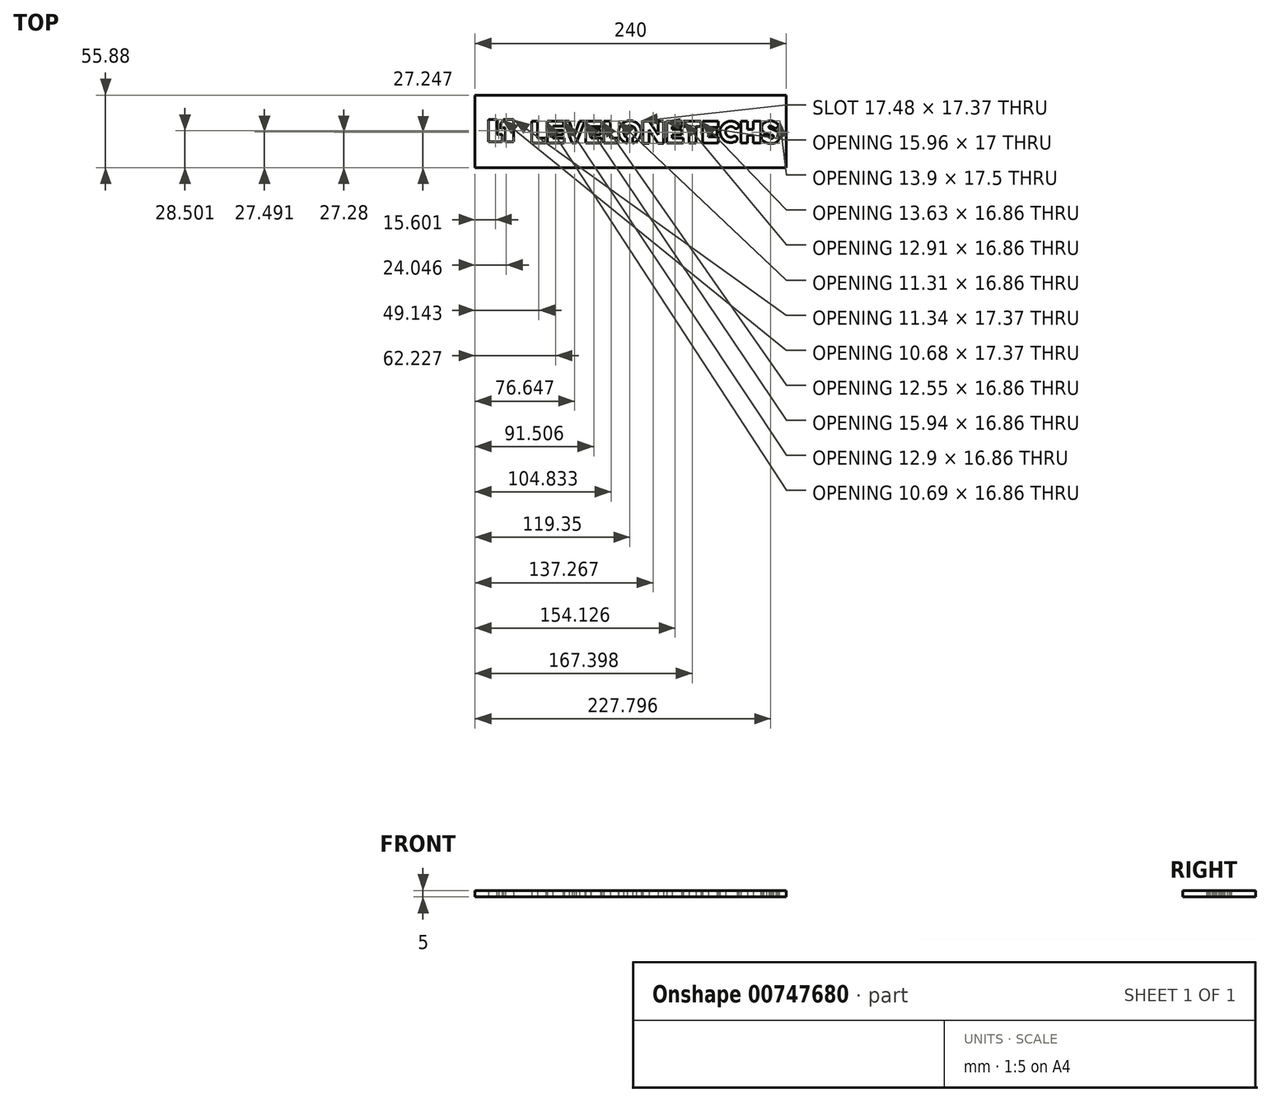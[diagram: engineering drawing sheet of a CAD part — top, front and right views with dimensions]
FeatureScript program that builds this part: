
annotation { "Feature Type Name" : "Feature", "Feature Type Description" : "" }
export const myFeature = defineFeature(function(context is Context, id is Id, definition is map)
    precondition{}
    {
        {
            var Q0;
            Q0=qCreatedBy(makeId("Top.planeOp"),FACE);
            var sketch = newSketch(context, id + "F0", { "sketchPlane" : qUnion([Q0])});
            skLineSegment(sketch, "E0.bottom", {"start": v(-121.3, 38.56) * mm, "end": v(118.7, 38.56) * mm});
            skLineSegment(sketch, "E0.top", {"start": v(-121.3, -17.32) * mm, "end": v(118.7, -17.32) * mm});
            skLineSegment(sketch, "E0.left", {"start": v(-121.3, 38.56) * mm, "end": v(-121.3, -17.32) * mm});
            skLineSegment(sketch, "E0.right", {"start": v(118.7, 38.56) * mm, "end": v(118.7, -17.32) * mm});
            skLineSegment(sketch, "E1", {"start": v(-77.5, 18.43) * mm, "end": v(-77.5, 1.57) * mm});
            skLineSegment(sketch, "E2", {"start": v(-77.5, 1.57) * mm, "end": v(-66.81, 1.57) * mm});
            skLineSegment(sketch, "E3", {"start": v(-66.81, 1.57) * mm, "end": v(-66.81, 5.44) * mm});
            skLineSegment(sketch, "E4", {"start": v(-66.81, 5.44) * mm, "end": v(-73.26, 5.44) * mm});
            skLineSegment(sketch, "E5", {"start": v(-73.26, 5.44) * mm, "end": v(-73.26, 18.43) * mm});
            skLineSegment(sketch, "E6", {"start": v(-73.26, 18.43) * mm, "end": v(-77.5, 18.43) * mm});
            skLineSegment(sketch, "E7", {"start": v(-65.52, 18.43) * mm, "end": v(-65.52, 1.57) * mm});
            skLineSegment(sketch, "E8", {"start": v(-65.52, 1.57) * mm, "end": v(-52.62, 1.57) * mm});
            skLineSegment(sketch, "E9", {"start": v(-52.62, 1.57) * mm, "end": v(-52.62, 5.44) * mm});
            skLineSegment(sketch, "E10", {"start": v(-52.62, 5.44) * mm, "end": v(-61.28, 5.44) * mm});
            skLineSegment(sketch, "E11", {"start": v(-61.28, 5.44) * mm, "end": v(-61.28, 8.02) * mm});
            skLineSegment(sketch, "E12", {"start": v(-61.28, 8.02) * mm, "end": v(-53.64, 8.02) * mm});
            skLineSegment(sketch, "E13", {"start": v(-53.64, 8.02) * mm, "end": v(-53.64, 11.61) * mm});
            skLineSegment(sketch, "E14", {"start": v(-53.64, 11.61) * mm, "end": v(-61.38, 11.61) * mm});
            skLineSegment(sketch, "E15", {"start": v(-61.38, 11.61) * mm, "end": v(-61.38, 14.56) * mm});
            skLineSegment(sketch, "E16", {"start": v(-61.38, 14.56) * mm, "end": v(-53.17, 14.56) * mm});
            skLineSegment(sketch, "E17", {"start": v(-53.17, 14.56) * mm, "end": v(-53.17, 18.43) * mm});
            skLineSegment(sketch, "E18", {"start": v(-53.17, 18.43) * mm, "end": v(-65.52, 18.43) * mm});
            skLineSegment(sketch, "E19", {"start": v(-52.62, 18.43) * mm, "end": v(-46.63, 1.57) * mm});
            skLineSegment(sketch, "E20", {"start": v(-46.63, 1.57) * mm, "end": v(-43.4, 1.57) * mm});
            skLineSegment(sketch, "E21", {"start": v(-43.4, 1.57) * mm, "end": v(-36.68, 18.43) * mm});
            skLineSegment(sketch, "E22", {"start": v(-36.68, 18.43) * mm, "end": v(-40.74, 18.43) * mm});
            skLineSegment(sketch, "E23", {"start": v(-40.74, 18.43) * mm, "end": v(-44.98, 7.19) * mm});
            skLineSegment(sketch, "E24", {"start": v(-44.98, 7.19) * mm, "end": v(-48.75, 18.43) * mm});
            skLineSegment(sketch, "E25", {"start": v(-48.75, 18.43) * mm, "end": v(-52.62, 18.43) * mm});
            skLineSegment(sketch, "E26", {"start": v(-36.07, 18.43) * mm, "end": v(-36.07, 1.57) * mm});
            skLineSegment(sketch, "E27", {"start": v(-36.07, 1.57) * mm, "end": v(-23.52, 1.57) * mm});
            skLineSegment(sketch, "E28", {"start": v(-23.52, 1.57) * mm, "end": v(-23.52, 5.44) * mm});
            skLineSegment(sketch, "E29", {"start": v(-23.52, 5.44) * mm, "end": v(-31.89, 5.44) * mm});
            skLineSegment(sketch, "E30", {"start": v(-31.89, 5.44) * mm, "end": v(-31.89, 7.83) * mm});
            skLineSegment(sketch, "E31", {"start": v(-31.89, 7.83) * mm, "end": v(-24.56, 7.83) * mm});
            skLineSegment(sketch, "E32", {"start": v(-24.56, 7.83) * mm, "end": v(-24.56, 11.98) * mm});
            skLineSegment(sketch, "E33", {"start": v(-24.56, 11.98) * mm, "end": v(-32.27, 11.98) * mm});
            skLineSegment(sketch, "E34", {"start": v(-32.27, 11.98) * mm, "end": v(-32.27, 14.34) * mm});
            skLineSegment(sketch, "E35", {"start": v(-32.27, 14.34) * mm, "end": v(-23.6, 14.34) * mm});
            skLineSegment(sketch, "E36", {"start": v(-23.6, 14.34) * mm, "end": v(-23.6, 18.43) * mm});
            skLineSegment(sketch, "E37", {"start": v(-23.6, 18.43) * mm, "end": v(-36.07, 18.43) * mm});
            skLineSegment(sketch, "E38", {"start": v(-111.04, 19.86) * mm, "end": v(-111.04, 2.5) * mm});
            skLineSegment(sketch, "E39", {"start": v(-111.04, 2.5) * mm, "end": v(-100.36, 2.5) * mm});
            skLineSegment(sketch, "E40", {"start": v(-100.36, 2.5) * mm, "end": v(-100.36, 8.47) * mm});
            skLineSegment(sketch, "E41", {"start": v(-100.36, 8.47) * mm, "end": v(-104.65, 8.47) * mm});
            skLineSegment(sketch, "E42", {"start": v(-104.65, 8.47) * mm, "end": v(-104.65, 19.86) * mm});
            skLineSegment(sketch, "E43", {"start": v(-104.65, 19.86) * mm, "end": v(-111.04, 19.86) * mm});
            skLineSegment(sketch, "E44", {"start": v(-91.58, 2.5) * mm, "end": v(-91.58, 19.86) * mm});
            skLineSegment(sketch, "E45", {"start": v(-91.58, 19.86) * mm, "end": v(-99.58, 19.86) * mm});
            skLineSegment(sketch, "E46", {"start": v(-99.58, 19.86) * mm, "end": v(-102.92, 13.24) * mm});
            skLineSegment(sketch, "E47", {"start": v(-102.92, 13.24) * mm, "end": v(-98.09, 13.24) * mm});
            skLineSegment(sketch, "E48", {"start": v(-98.09, 13.24) * mm, "end": v(-98.09, 2.5) * mm});
            skLineSegment(sketch, "E49", {"start": v(-98.09, 2.5) * mm, "end": v(-91.58, 2.5) * mm});
            skLineSegment(sketch, "E50", {"start": v(-22.12, 18.43) * mm, "end": v(-22.12, 1.57) * mm});
            skLineSegment(sketch, "E51", {"start": v(-22.12, 1.57) * mm, "end": v(-10.81, 1.57) * mm});
            skLineSegment(sketch, "E52", {"start": v(-10.81, 1.57) * mm, "end": v(-10.81, 5.46) * mm});
            skLineSegment(sketch, "E53", {"start": v(-10.81, 5.46) * mm, "end": v(-16.93, 5.46) * mm});
            skLineSegment(sketch, "E54", {"start": v(-16.93, 5.46) * mm, "end": v(-16.93, 18.43) * mm});
            skLineSegment(sketch, "E55", {"start": v(-16.93, 18.43) * mm, "end": v(-22.12, 18.43) * mm});
            skArc(sketch, "E56", {"start": v(0, 5.61) * mm, "mid": v(-1.94, 14.92) * mm, "end": v(-3.92, 5.62) * mm});
            skArc(sketch, "E57", {"start": v(0, 1.49) * mm, "mid": v(-1.94, 18.86) * mm, "end": v(-3.92, 1.5) * mm});
            skLineSegment(sketch, "E58.left", {"start": v(-3.92, 5.62) * mm, "end": v(-3.92, 1.5) * mm});
            skLineSegment(sketch, "E58.right", {"start": v(0, 5.62) * mm, "end": v(0, 1.49) * mm});
            skPoint(sketch, "E59.orphan", {"position": v(0, 1.07) * mm});
            skLineSegment(sketch, "E60", {"start": v(7.99, 1.43) * mm, "end": v(7.99, 18.43) * mm});
            skLineSegment(sketch, "E61", {"start": v(7.99, 18.43) * mm, "end": v(12.76, 18.43) * mm});
            skLineSegment(sketch, "E62", {"start": v(12.76, 18.43) * mm, "end": v(19.85, 7.97) * mm});
            skLineSegment(sketch, "E63", {"start": v(19.85, 7.97) * mm, "end": v(19.85, 18.43) * mm});
            skLineSegment(sketch, "E64", {"start": v(19.85, 18.43) * mm, "end": v(23.94, 18.35) * mm});
            skLineSegment(sketch, "E65", {"start": v(23.94, 18.35) * mm, "end": v(23.94, 1.43) * mm});
            skLineSegment(sketch, "E66", {"start": v(23.94, 1.43) * mm, "end": v(19.85, 1.43) * mm});
            skLineSegment(sketch, "E67", {"start": v(19.85, 1.43) * mm, "end": v(12.76, 11.89) * mm});
            skLineSegment(sketch, "E68", {"start": v(12.76, 11.89) * mm, "end": v(12.76, 1.43) * mm});
            skLineSegment(sketch, "E69", {"start": v(12.76, 1.43) * mm, "end": v(7.99, 1.43) * mm});
            skLineSegment(sketch, "E70", {"start": v(26.37, 18.43) * mm, "end": v(26.37, 1.57) * mm});
            skPoint(sketch, "E70.endSnap0", {"position": v(-16.47, 1.57) * mm});
            skLineSegment(sketch, "E71", {"start": v(26.37, 1.57) * mm, "end": v(39.28, 1.57) * mm});
            skLineSegment(sketch, "E72", {"start": v(39.28, 1.57) * mm, "end": v(39.28, 5.55) * mm});
            skLineSegment(sketch, "E73", {"start": v(39.28, 5.55) * mm, "end": v(30.5, 5.55) * mm});
            skLineSegment(sketch, "E74", {"start": v(30.5, 5.55) * mm, "end": v(30.5, 7.97) * mm});
            skLineSegment(sketch, "E75", {"start": v(30.5, 7.97) * mm, "end": v(38.02, 7.97) * mm});
            skLineSegment(sketch, "E76", {"start": v(38.02, 7.97) * mm, "end": v(38.02, 12.05) * mm});
            skLineSegment(sketch, "E77", {"start": v(38.02, 12.05) * mm, "end": v(30.57, 12.05) * mm});
            skLineSegment(sketch, "E78", {"start": v(30.57, 12.05) * mm, "end": v(30.57, 14.25) * mm});
            skLineSegment(sketch, "E79", {"start": v(30.57, 14.25) * mm, "end": v(38.35, 14.25) * mm});
            skLineSegment(sketch, "E80", {"start": v(38.35, 14.25) * mm, "end": v(38.35, 18.43) * mm});
            skLineSegment(sketch, "E81", {"start": v(38.35, 18.43) * mm, "end": v(26.37, 18.43) * mm});
            skLineSegment(sketch, "E82", {"start": v(39.28, 18.43) * mm, "end": v(39.28, 14.25) * mm});
            skLineSegment(sketch, "E83", {"start": v(39.28, 14.25) * mm, "end": v(43.53, 14.25) * mm});
            skLineSegment(sketch, "E84", {"start": v(43.53, 14.25) * mm, "end": v(43.53, 1.57) * mm});
            skLineSegment(sketch, "E85", {"start": v(43.53, 1.57) * mm, "end": v(48.96, 1.57) * mm});
            skLineSegment(sketch, "E86", {"start": v(48.96, 1.57) * mm, "end": v(48.96, 14.25) * mm});
            skLineSegment(sketch, "E87", {"start": v(48.96, 14.25) * mm, "end": v(52.91, 14.25) * mm});
            skLineSegment(sketch, "E88", {"start": v(52.91, 14.25) * mm, "end": v(52.91, 18.43) * mm});
            skLineSegment(sketch, "E89", {"start": v(52.91, 18.43) * mm, "end": v(39.28, 18.43) * mm});
            skLineSegment(sketch, "E90", {"start": v(54.12, 18.43) * mm, "end": v(54.12, 1.57) * mm});
            skLineSegment(sketch, "E91", {"start": v(54.12, 1.57) * mm, "end": v(66.21, 1.57) * mm});
            skLineSegment(sketch, "E92", {"start": v(66.21, 1.57) * mm, "end": v(66.21, 6.54) * mm});
            skLineSegment(sketch, "E93", {"start": v(66.21, 6.54) * mm, "end": v(58.66, 6.54) * mm});
            skLineSegment(sketch, "E94", {"start": v(58.66, 6.54) * mm, "end": v(58.66, 7.8) * mm});
            skLineSegment(sketch, "E95", {"start": v(58.66, 7.8) * mm, "end": v(65.13, 7.8) * mm});
            skLineSegment(sketch, "E96", {"start": v(65.13, 7.8) * mm, "end": v(65.13, 12.05) * mm});
            skLineSegment(sketch, "E97", {"start": v(65.13, 12.05) * mm, "end": v(58.68, 12.05) * mm});
            skLineSegment(sketch, "E98", {"start": v(58.68, 12.05) * mm, "end": v(58.68, 13.64) * mm});
            skLineSegment(sketch, "E99", {"start": v(58.68, 13.64) * mm, "end": v(66.24, 13.64) * mm});
            skLineSegment(sketch, "E100", {"start": v(66.24, 13.64) * mm, "end": v(66.24, 18.43) * mm});
            skLineSegment(sketch, "E101", {"start": v(66.24, 18.43) * mm, "end": v(54.12, 18.43) * mm});
            skArc(sketch, "E102", {"start": v(78.55, 13.3) * mm, "mid": v(71.8, 10.7) * mm, "end": v(77.83, 6.71) * mm});
            skArc(sketch, "E103", {"start": v(81.33, 16.43) * mm, "mid": v(67.64, 11.15) * mm, "end": v(79.88, 3.06) * mm});
            skArc(sketch, "E104", {"start": v(78.55, 13.3) * mm, "mid": v(81.5, 13.47) * mm, "end": v(81.33, 16.43) * mm});
            skArc(sketch, "E105", {"start": v(79.88, 3.06) * mm, "mid": v(80.69, 5.91) * mm, "end": v(77.83, 6.71) * mm});
            skLineSegment(sketch, "E106.bottom", {"start": v(83.7, 18.43) * mm, "end": v(88.82, 18.43) * mm});
            skLineSegment(sketch, "E106.top", {"start": v(83.7, 1.57) * mm, "end": v(88.82, 1.57) * mm});
            skLineSegment(sketch, "E106.left", {"start": v(83.7, 18.43) * mm, "end": v(83.7, 1.57) * mm});
            skLineSegment(sketch, "E106.right", {"start": v(88.82, 18.43) * mm, "end": v(88.82, 12.02) * mm});
            skLineSegment(sketch, "E107.bottom", {"start": v(93.33, 18.43) * mm, "end": v(98.75, 18.43) * mm});
            skLineSegment(sketch, "E107.top", {"start": v(93.33, 1.57) * mm, "end": v(98.75, 1.57) * mm});
            skLineSegment(sketch, "E107.left", {"start": v(93.33, 18.43) * mm, "end": v(93.33, 12.02) * mm});
            skLineSegment(sketch, "E107.right", {"start": v(98.75, 18.43) * mm, "end": v(98.75, 1.57) * mm});
            skLineSegment(sketch, "E108.bottom", {"start": v(88.82, 12.02) * mm, "end": v(93.33, 12.02) * mm});
            skLineSegment(sketch, "E108.top", {"start": v(88.82, 7.7) * mm, "end": v(93.33, 7.7) * mm});
            skLineSegment(sketch, "E109.trimOffspring", {"start": v(88.82, 7.7) * mm, "end": v(88.82, 1.57) * mm});
            skLineSegment(sketch, "E110.trimOffspring", {"start": v(93.33, 7.7) * mm, "end": v(93.33, 1.57) * mm});
            skFitSpline(sketch, "E111", {"points": [v(101.2, 16.73) * mm, v(111.69, 16.68) * mm], "startDerivative": vector(7.27, 7.48) * mm, "endDerivative": vector(9.04, -8.59) * mm});
            skFitSpline(sketch, "E112", {"points": [v(101.2, 16.73) * mm, v(101.2, 10.2) * mm], "startDerivative": vector(-5.67, -4.48) * mm, "endDerivative": vector(6.41, -4.8) * mm});
            skFitSpline(sketch, "E113", {"points": [v(101.2, 10.2) * mm, v(107.5, 7.79) * mm], "startDerivative": vector(6, -4.4) * mm, "endDerivative": vector(6.5, -0.05) * mm});
            skFitSpline(sketch, "E114", {"points": [v(107.5, 7.79) * mm, v(106.35, 5.59) * mm], "startDerivative": vector(7.72, -0.15) * mm, "endDerivative": vector(-6.84, 4.4) * mm});
            skFitSpline(sketch, "E115", {"points": [v(100.31, 3.55) * mm, v(112.6, 3.62) * mm], "startDerivative": vector(11.68, -9.48) * mm, "endDerivative": vector(7.67, 9.53) * mm});
            skFitSpline(sketch, "E116", {"points": [v(100.31, 3.55) * mm, v(103.47, 7.51) * mm], "startDerivative": vector(-5.38, 5.03) * mm, "endDerivative": vector(10.7, -4.2) * mm});
            skLineSegment(sketch, "E117", {"start": v(103.47, 7.51) * mm, "end": v(106.35, 5.59) * mm});
            skFitSpline(sketch, "E118", {"points": [v(112.6, 3.62) * mm, v(110.56, 11.03) * mm], "startDerivative": vector(3.57, 4.5) * mm, "endDerivative": vector(-11.1, 3.62) * mm});
            skFitSpline(sketch, "E119", {"points": [v(111.69, 16.68) * mm, v(108.8, 13.62) * mm], "startDerivative": vector(6, -5.85) * mm, "endDerivative": vector(-7.43, 5.33) * mm});
            skFitSpline(sketch, "E120", {"points": [v(108.8, 13.62) * mm, v(105.31, 14.47) * mm], "startDerivative": vector(-4.1, 3.47) * mm, "endDerivative": vector(-1.22, -2.64) * mm});
            skFitSpline(sketch, "E121", {"points": [v(105.31, 14.47) * mm, v(110.56, 11.03) * mm], "startDerivative": vector(-3.71, -5.62) * mm, "endDerivative": vector(5.24, -3.44) * mm});
            skSolve(sketch);
        }
        {
            var Q0;
            Q0 = qSketchRegion(id + "F0", true);
            extrude(context, id + "F1", {"entities" : qUnion([Q0]), "depth" : 5 * mm, "offsetDistance" : 25.4 * mm});
        }
    });
